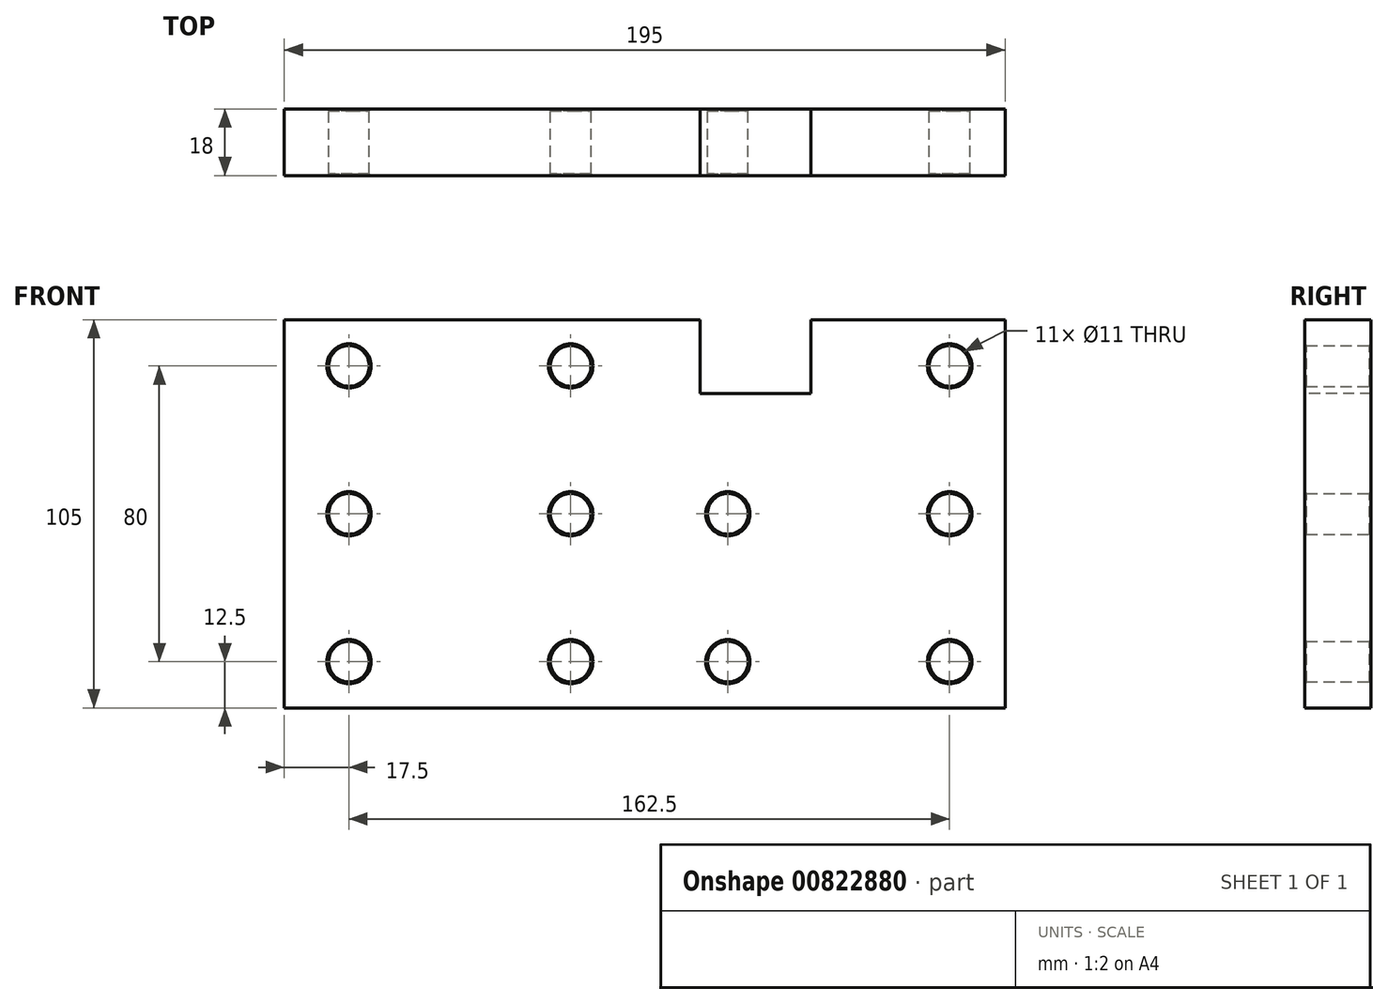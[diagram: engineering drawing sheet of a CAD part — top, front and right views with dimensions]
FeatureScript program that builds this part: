
annotation { "Feature Type Name" : "Feature", "Feature Type Description" : "" }
export const myFeature = defineFeature(function(context is Context, id is Id, definition is map)
    precondition{}
    {
        {
            var Q0;
            Q0=qCreatedBy(makeId("Front.planeOp"),FACE);
            var sketch = newSketch(context, id + "F0", { "sketchPlane" : qUnion([Q0])});
            skLineSegment(sketch, "E0.bottom", {"start": v(-97.5, -52.5) * mm, "end": v(97.5, -52.5) * mm});
            skLineSegment(sketch, "E0.top", {"start": v(-97.5, 52.5) * mm, "end": v(97.5, 52.5) * mm});
            skLineSegment(sketch, "E0.left", {"start": v(-97.5, -52.5) * mm, "end": v(-97.5, 52.5) * mm});
            skLineSegment(sketch, "E0.right", {"start": v(97.5, -52.5) * mm, "end": v(97.5, 52.5) * mm});
            skPoint(sketch, "E0.middle", {"position": v(0, 0) * mm});
            skLineSegment(sketch, "E1", {"start": v(-50, 0) * mm, "end": v(0, 0) * mm, "construction": true});
            skLineSegment(sketch, "E2", {"start": v(0, 0) * mm, "end": v(52.5, 0) * mm, "construction": true});
            skLineSegment(sketch, "E3.bottom", {"start": v(-20, 40) * mm, "end": v(-80, 40) * mm, "construction": true});
            skLineSegment(sketch, "E3.top", {"start": v(-20, -40) * mm, "end": v(-80, -40) * mm, "construction": true});
            skLineSegment(sketch, "E3.left", {"start": v(-20, 40) * mm, "end": v(-20, -40) * mm, "construction": true});
            skLineSegment(sketch, "E3.right", {"start": v(-80, 40) * mm, "end": v(-80, -40) * mm, "construction": true});
            skPoint(sketch, "E3.middle", {"position": v(-50, 0) * mm});
            skLineSegment(sketch, "E4.bottom", {"start": v(22.5, 40) * mm, "end": v(82.5, 40) * mm, "construction": true});
            skLineSegment(sketch, "E4.top", {"start": v(22.5, -40) * mm, "end": v(82.5, -40) * mm, "construction": true});
            skLineSegment(sketch, "E4.left", {"start": v(22.5, 40) * mm, "end": v(22.5, -40) * mm, "construction": true});
            skLineSegment(sketch, "E4.right", {"start": v(82.5, 40) * mm, "end": v(82.5, -40) * mm, "construction": true});
            skPoint(sketch, "E4.middle", {"position": v(52.5, 0) * mm});
            skLineSegment(sketch, "E5", {"start": v(-80, 0) * mm, "end": v(-20, 0) * mm, "construction": true});
            skLineSegment(sketch, "E6", {"start": v(82.5, 0) * mm, "end": v(22.5, 0) * mm, "construction": true});
            skCircle(sketch, "E7", {"center": v(-80, 40) * mm, "radius": 5.5 * mm});
            skCircle(sketch, "E8", {"center": v(22.5, 40) * mm, "radius": 5.5 * mm, "construction": true});
            skCircle(sketch, "E9.0.1.0", {"center": v(-80, 0) * mm, "radius": 5.5 * mm});
            skCircle(sketch, "E9.0.1.1", {"center": v(22.5, 0) * mm, "radius": 5.5 * mm});
            skCircle(sketch, "E9.0.2.0", {"center": v(-80, -40) * mm, "radius": 5.5 * mm});
            skCircle(sketch, "E9.0.2.1", {"center": v(22.5, -40) * mm, "radius": 5.5 * mm});
            skCircle(sketch, "E9.1.0.0", {"center": v(-20, 40) * mm, "radius": 5.5 * mm});
            skCircle(sketch, "E9.1.0.1", {"center": v(82.5, 40) * mm, "radius": 5.5 * mm});
            skCircle(sketch, "E9.1.1.0", {"center": v(-20, 0) * mm, "radius": 5.5 * mm});
            skCircle(sketch, "E9.1.1.1", {"center": v(82.5, 0) * mm, "radius": 5.5 * mm});
            skCircle(sketch, "E9.1.2.0", {"center": v(-20, -40) * mm, "radius": 5.5 * mm});
            skCircle(sketch, "E9.1.2.1", {"center": v(82.5, -40) * mm, "radius": 5.5 * mm});
            skLineSegment(sketch, "E9.direction1", {"start": v(-80, 40) * mm, "end": v(-20, 40) * mm, "construction": true});
            skLineSegment(sketch, "E9.direction2", {"start": v(-80, 40) * mm, "end": v(-80, 0) * mm, "construction": true});
            skLineSegment(sketch, "E10", {"start": v(0, 0) * mm, "end": v(0, 76.2) * mm, "construction": true});
            skLineSegment(sketch, "E11", {"start": v(0, 76.2) * mm, "end": v(60.65, 76.2) * mm, "construction": true});
            skCircle(sketch, "E12", {"center": v(30, 50.2) * mm, "radius": 12.5 * mm, "construction": true});
            skLineSegment(sketch, "E13", {"start": v(30, 50.2) * mm, "end": v(30, 72.34) * mm, "construction": true});
            skLineSegment(sketch, "E14.bottom", {"start": v(45, 112.17) * mm, "end": v(15, 112.17) * mm});
            skLineSegment(sketch, "E14.top", {"start": v(45, 32.5) * mm, "end": v(15, 32.5) * mm});
            skLineSegment(sketch, "E14.left", {"start": v(45, 112.17) * mm, "end": v(45, 32.5) * mm});
            skLineSegment(sketch, "E14.right", {"start": v(15, 112.17) * mm, "end": v(15, 32.5) * mm});
            skPoint(sketch, "E14.middle", {"position": v(30, 72.34) * mm});
            skSolve(sketch);
        }
        {
            var Q0;
            Q0=qSketchRegion(id+"F0",true);
            extrude(context, id + "F1", {"entities" : qUnion([Q0]), "depth" : 18 * mm, "offsetDistance" : 25 * mm});
        }
        {
            var Q0;
            Q0=makeQuery(id+"F1.opExtrude","SWEPT_FACE",FACE,{"disambiguationData":[OSD([sQuery(id+"F0.wireOp",EDGE,"E7")])]});
            var Q1;
            Q1=makeQuery(id+"F1.opExtrude","SWEPT_FACE",FACE,{"disambiguationData":[OSD([sQuery(id+"F0.wireOp",EDGE,"E9.0.1.0")])]});
            var Q2;
            Q2=makeQuery(id+"F1.opExtrude","SWEPT_FACE",FACE,{"disambiguationData":[OSD([sQuery(id+"F0.wireOp",EDGE,"E9.0.2.0")])]});
            var Q3;
            Q3=makeQuery(id+"F1.opExtrude","SWEPT_FACE",FACE,{"disambiguationData":[OSD([sQuery(id+"F0.wireOp",EDGE,"E9.1.0.0")])]});
            var Q4;
            Q4=makeQuery(id+"F1.opExtrude","SWEPT_FACE",FACE,{"disambiguationData":[OSD([sQuery(id+"F0.wireOp",EDGE,"E9.1.1.0")])]});
            var Q5;
            Q5=makeQuery(id+"F1.opExtrude","SWEPT_FACE",FACE,{"disambiguationData":[OSD([sQuery(id+"F0.wireOp",EDGE,"E9.1.2.0")])]});
            var Q6;
            Q6=makeQuery(id+"F1.opExtrude","SWEPT_FACE",FACE,{"disambiguationData":[OSD([sQuery(id+"F0.wireOp",EDGE,"E8")])]});
            var Q7;
            Q7=makeQuery(id+"F1.opExtrude","SWEPT_FACE",FACE,{"disambiguationData":[OSD([sQuery(id+"F0.wireOp",EDGE,"E9.0.1.1")])]});
            var Q8;
            Q8=makeQuery(id+"F1.opExtrude","SWEPT_FACE",FACE,{"disambiguationData":[OSD([sQuery(id+"F0.wireOp",EDGE,"E9.0.2.1")])]});
            var Q9;
            Q9=makeQuery(id+"F1.opExtrude","SWEPT_FACE",FACE,{"disambiguationData":[OSD([sQuery(id+"F0.wireOp",EDGE,"E9.1.0.1")])]});
            var Q10;
            Q10=makeQuery(id+"F1.opExtrude","SWEPT_FACE",FACE,{"disambiguationData":[OSD([sQuery(id+"F0.wireOp",EDGE,"E9.1.1.1")])]});
            var Q11;
            Q11=makeQuery(id+"F1.opExtrude","SWEPT_FACE",FACE,{"disambiguationData":[OSD([sQuery(id+"F0.wireOp",EDGE,"E9.1.2.1")])]});
            chamfer(context, id + "F2", {"entities" : qUnion([Q0, Q1, Q2, Q3, Q4, Q5, Q6, Q7, Q8, Q9, Q10, Q11]), "width" : 0.5 * mm, "tangentPropagation" : true});
        }
        {
            var Q0;
            Q0=makeQuery(id+"F1.opExtrude","CAP_FACE",FACE,{"disambiguationData":[OSD([sQuery(id+"F0.wireOp",EDGE,"E0.bottom"),sQuery(id+"F0.wireOp",EDGE,"E0.top"),sQuery(id+"F0.wireOp",EDGE,"E0.left"),sQuery(id+"F0.wireOp",EDGE,"E0.right"),sQuery(id+"F0.wireOp",EDGE,"E7"),sQuery(id+"F0.wireOp",EDGE,"E9.0.1.0"),sQuery(id+"F0.wireOp",EDGE,"E9.0.1.1"),sQuery(id+"F0.wireOp",EDGE,"E9.0.2.0"),sQuery(id+"F0.wireOp",EDGE,"E9.0.2.1"),sQuery(id+"F0.wireOp",EDGE,"E9.1.0.0"),sQuery(id+"F0.wireOp",EDGE,"E9.1.0.1"),sQuery(id+"F0.wireOp",EDGE,"E9.1.1.0"),sQuery(id+"F0.wireOp",EDGE,"E9.1.1.1"),sQuery(id+"F0.wireOp",EDGE,"E9.1.2.0"),sQuery(id+"F0.wireOp",EDGE,"E9.1.2.1"),sQuery(id+"F0.wireOp",EDGE,"E14.bottom"),sQuery(id+"F0.wireOp",EDGE,"E14.left"),sQuery(id+"F0.wireOp",EDGE,"E14.right")])],"isStart":false});
            var sketch = newSketch(context, id + "F3", { "sketchPlane" : qUnion([Q0])});
            skLineSegment(sketch, "E15.0", {"start": v(15, 112.17) * mm, "end": v(15, 32.5) * mm});
            skLineSegment(sketch, "E16.0", {"start": v(45, 32.5) * mm, "end": v(15, 32.5) * mm});
            skLineSegment(sketch, "E17.0", {"start": v(45, 112.17) * mm, "end": v(45, 32.5) * mm});
            skLineSegment(sketch, "E18.0", {"start": v(45, 112.17) * mm, "end": v(15, 112.17) * mm});
            skSolve(sketch);
        }
        {
            var Q0;
            Q0 = qSketchRegion(id + "F3", true);
            extrude(context, id + "F4", {"entities" : qUnion([Q0]), "operationType" : NewBodyOperationType.REMOVE, "oppositeDirection" : true, "depth" : 25 * mm, "offsetDistance" : 25 * mm});
        }
    });
